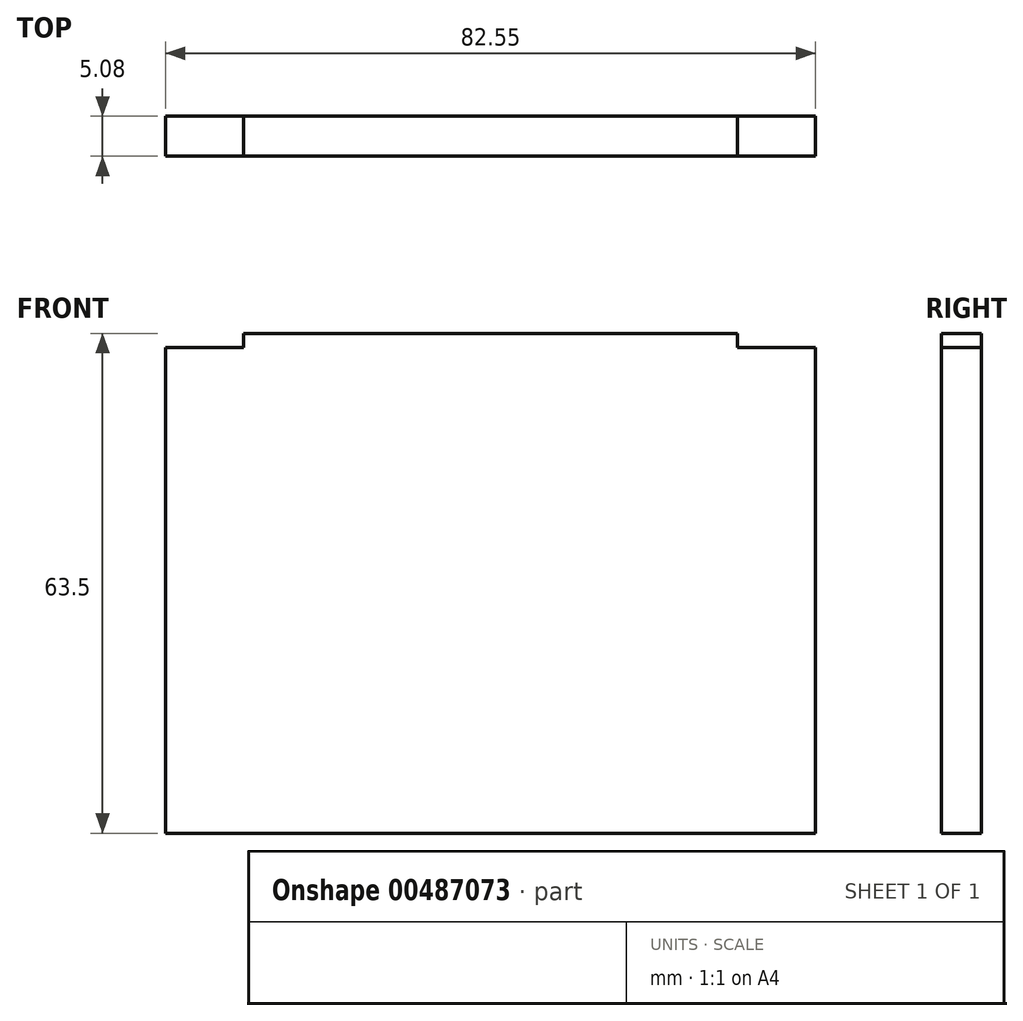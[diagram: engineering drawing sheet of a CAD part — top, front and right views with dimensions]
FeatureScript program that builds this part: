
annotation { "Feature Type Name" : "Feature", "Feature Type Description" : "" }
export const myFeature = defineFeature(function(context is Context, id is Id, definition is map)
    precondition{}
    {
        {
            var Q0;
            Q0=qCreatedBy(makeId("Front.planeOp"),FACE);
            var sketch = newSketch(context, id + "F0", { "sketchPlane" : qUnion([Q0])});
            skLineSegment(sketch, "E0.bottom", {"start": v(-37, 41.32) * mm, "end": v(25.74, 41.32) * mm});
            skLineSegment(sketch, "E0.top", {"start": v(-46.9, -22.18) * mm, "end": v(35.65, -22.18) * mm});
            skLineSegment(sketch, "E0.left", {"start": v(-46.9, 39.54) * mm, "end": v(-46.9, -22.18) * mm});
            skLineSegment(sketch, "E0.right", {"start": v(35.65, 39.54) * mm, "end": v(35.65, -22.18) * mm});
            skLineSegment(sketch, "E1.top", {"start": v(-46.9, 39.54) * mm, "end": v(-37, 39.54) * mm});
            skLineSegment(sketch, "E1.right", {"start": v(-37, 41.32) * mm, "end": v(-37, 39.54) * mm});
            skLineSegment(sketch, "E2.top", {"start": v(35.65, 39.54) * mm, "end": v(25.74, 39.54) * mm});
            skLineSegment(sketch, "E2.right", {"start": v(25.74, 41.32) * mm, "end": v(25.74, 39.54) * mm});
            skSolve(sketch);
        }
        {
            var Q0;
            Q0 = qSketchRegion(id + "F0", true);
            extrude(context, id + "F1", {"entities" : qUnion([Q0]), "depth" : 5.08 * mm});
        }
    });
